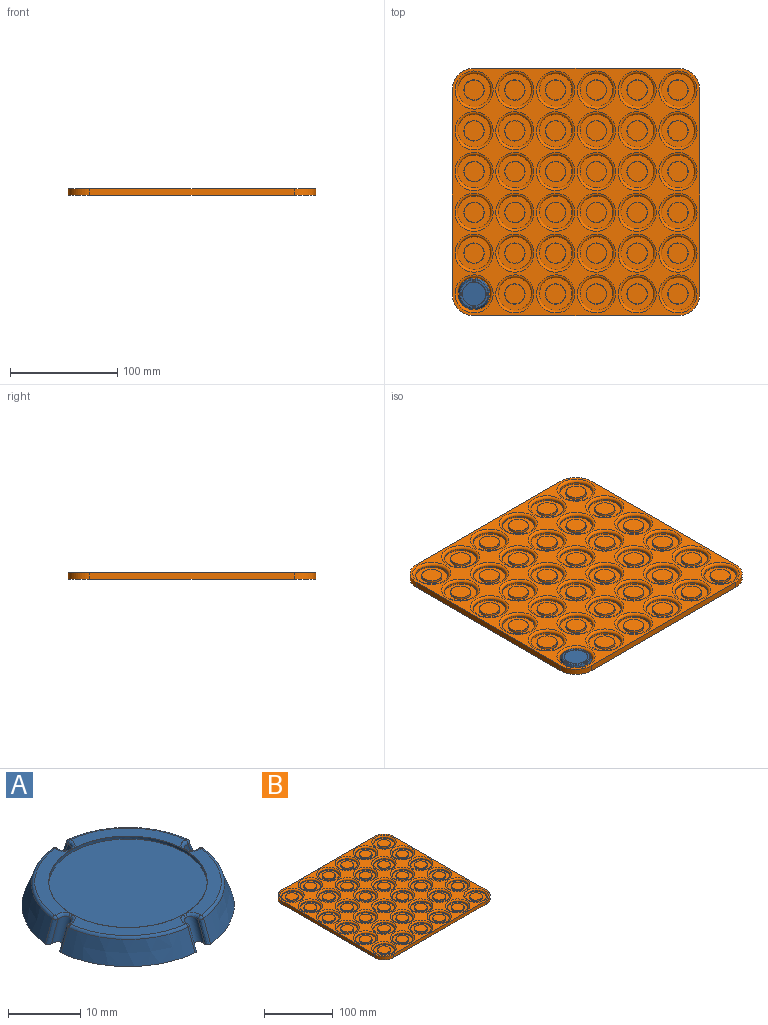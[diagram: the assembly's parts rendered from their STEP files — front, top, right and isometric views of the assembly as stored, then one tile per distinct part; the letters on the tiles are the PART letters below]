
ASSEMBLY  parts=2 mates=1
PART A: 82 faces, bbox 34.2x34.2x13 mm
  f0: cylinder r=3.5mm len=5.05mm, axis (0,-0.34,0.94), area 7.4mm2, adj f1,f32,f33,f34
  f1: bspline ~11.4x4.62mm, area 1.5mm2, adj f0,f2,f31,f34
  f2: sphere r=1mm, area 0.2mm2, adj f1,f3,f32
  f3: torus R=10.66mm, axis (0,0,1), area 13.1mm2, adj f2,f4,f5,f30,f31
  f4: sphere r=1mm, area 0.3mm2, adj f3,f32
  f5: plane 20.32x20.32mm, normal (0,0,-1), area 322.5mm2, adj f3,f6,f24,f25,f27,f28,f29,f32
  f6: torus R=10.66mm, axis (0,0,1), area 13.1mm2, adj f5,f7,f13,f23
  f7: sphere r=1mm, area 0.9mm2, adj f6,f8,f24
  f8: bspline ~11.4x4.62mm, area 1.5mm2, adj f7,f9,f13,f34
  f9: cylinder r=3.5mm len=5.05mm, axis (-0.34,0,0.94), area 7.4mm2, adj f8,f10,f24,f34
  f10: bspline ~11.4x4.62mm, area 1.5mm2, adj f9,f11,f12,f34
  f11: sphere r=1mm, area 0.8mm2, adj f10,f24,f25
  f12: cone r=12.4mm half-angle=20deg, axis (0,0,-1), area 16.4mm2, adj f10,f25,f33,f34
  f13: cone r=12.4mm half-angle=20deg, axis (0,0,-1), area 16.4mm2, adj f6,f8,f14,f34
  f14: bspline ~11.4x4.62mm, area 1.5mm2, adj f13,f15,f23,f34
  f15: cylinder r=3.5mm len=5.05mm, axis (0,0.34,0.94), area 7.4mm2, adj f14,f16,f29,f34
  f16: bspline ~11.4x4.62mm, area 1.5mm2, adj f15,f17,f22,f34
  f17: cone r=12.4mm half-angle=20deg, axis (0,0,-1), area 16.4mm2, adj f16,f18,f28,f34
  f18: bspline ~11.4x4.62mm, area 1.5mm2, adj f17,f19,f21,f34
  f19: cylinder r=3.5mm len=5.05mm, axis (0.34,0,0.94), area 7.4mm2, adj f18,f20,f27,f34
  f20: bspline ~11.4x4.62mm, area 1.5mm2, adj f19,f30,f31,f34
  f21: sphere r=1mm, area 0.4mm2, adj f18,f27,f28
  f22: sphere r=1mm, area 1.2mm2, adj f16,f28,f29
  f23: sphere r=1mm, area 0.4mm2, adj f6,f14,f29
  f24: bspline ~6.46x2.11mm, area 8mm2, adj f5,f7,f9,f11
  f25: torus R=10.66mm, axis (0,0,1), area 13.1mm2, adj f5,f11,f12,f26
  f26: sphere r=1mm, area 0.8mm2, adj f25,f32,f33
  f27: bspline ~6.46x2.11mm, area 8mm2, adj f5,f19,f21,f30
  f28: torus R=10.66mm, axis (0,0,1), area 13.1mm2, adj f5,f17,f21,f22
  f29: bspline ~6.46x2.11mm, area 8mm2, adj f5,f15,f22,f23
  f30: sphere r=1mm, area 1.2mm2, adj f3,f20,f27
  f31: cone r=12.4mm half-angle=20deg, axis (0,0,-1), area 16.4mm2, adj f1,f3,f20,f34
  f32: bspline ~6.46x2.11mm, area 8mm2, adj f0,f2,f4,f5,f26
  f33: bspline ~11.4x4.62mm, area 1.5mm2, adj f0,f12,f26,f34
  f34: plane 30.13x30.13mm, normal (0,0,-1), area 242.1mm2, adj f0,f1,f8,f9,f10,f12,f13,f14
  f35: cylinder r=1mm len=4.47mm, axis (0.34,0,0.94), area 13.2mm2, adj f34,f36,f65,f66,f67,f81
  f36: bspline ~1.87x1.6mm, area 1.4mm2, adj f35,f37,f64,f66
  f37: plane 12.6x12.6mm, normal (0,0,1), area 31.6mm2, adj f36,f38,f60,f63
  f38: bspline ~1.87x1.6mm, area 1.4mm2, adj f37,f39,f40,f78
  f39: sphere r=0.5mm, area 0.5mm2, adj f38,f63,f79
  f40: bspline ~0.76x0.5mm, area 0.2mm2, adj f38,f41,f60,f78
  f41: bspline ~1.87x1.6mm, area 1.4mm2, adj f40,f42,f59,f78
  f42: plane 12.6x12.6mm, normal (0,0,1), area 31.6mm2, adj f41,f43,f45,f60
  f43: torus R=12.94mm, axis (0,0,1), area 10.8mm2, adj f42,f44,f59,f76
  f44: sphere r=0.5mm, area 0.4mm2, adj f43,f45,f75
  f45: bspline ~1.87x1.6mm, area 1.4mm2, adj f42,f44,f46,f74
  f46: bspline ~0.76x0.5mm, area 0.2mm2, adj f45,f47,f60,f74
  f47: bspline ~1.87x1.6mm, area 1.4mm2, adj f46,f48,f58,f74
  f48: plane 12.6x12.6mm, normal (0,0,1), area 31.6mm2, adj f47,f49,f57,f60
  f49: bspline ~1.87x1.6mm, area 1.4mm2, adj f48,f50,f56,f70
  f50: bspline ~0.76x0.5mm, area 0.2mm2, adj f49,f51,f60,f70
  f51: bspline ~1.87x1.6mm, area 1.4mm2, adj f50,f52,f55,f70
  f52: sphere r=0.5mm, area 0.4mm2, adj f51,f53,f69
  f53: torus R=12.94mm, axis (0,0,1), area 10.8mm2, adj f52,f54,f55,f68
  f54: sphere r=0.5mm, area 0.6mm2, adj f53,f65,f67
  f55: plane 12.6x12.6mm, normal (0,0,1), area 31.6mm2, adj f51,f53,f60,f65
  f56: sphere r=0.5mm, area 0.4mm2, adj f49,f57,f71
  f57: torus R=12.94mm, axis (0,0,1), area 10.8mm2, adj f48,f56,f58,f72
  f58: sphere r=0.5mm, area 0.3mm2, adj f47,f57,f73
  f59: sphere r=0.5mm, area 0.5mm2, adj f41,f43,f77
  f60: torus R=0.26mm, axis (0,0,-1), area 1.1mm2, adj f37,f40,f42,f46,f48,f50,f55,f61
  f61: cylinder r=11mm len=22mm, axis (0,0,-1), area 35mm2, adj f60,f62
  f62: plane 22x22mm, normal (0,0,1), area 380.1mm2, adj f61
  f63: torus R=12.94mm, axis (0,0,1), area 10.8mm2, adj f37,f39,f64,f80
  f64: sphere r=0.5mm, area 0.4mm2, adj f36,f63,f81
  f65: bspline ~1.87x1.6mm, area 1.4mm2, adj f35,f54,f55,f66
  f66: bspline ~0.76x0.5mm, area 0.2mm2, adj f35,f36,f60,f65
  f67: bspline ~5.86x2.67mm, area 3.5mm2, adj f34,f35,f54,f68
  f68: cone r=14.75mm half-angle=20deg, axis (0,0,-1), area 74.4mm2, adj f34,f53,f67,f69
  f69: bspline ~10.56x4.38mm, area 3.5mm2, adj f34,f52,f68,f70
  f70: cylinder r=1mm len=4.47mm, axis (0,0.34,0.94), area 13.2mm2, adj f34,f49,f50,f51,f69,f71
  f71: bspline ~5.86x2.67mm, area 3.5mm2, adj f34,f56,f70,f72
  f72: cone r=14.75mm half-angle=20deg, axis (0,0,-1), area 74.4mm2, adj f34,f57,f71,f73
  f73: bspline ~10.56x4.38mm, area 3.5mm2, adj f34,f58,f72,f74
  f74: cylinder r=1mm len=4.47mm, axis (-0.34,0,0.94), area 13.2mm2, adj f34,f45,f46,f47,f73,f75
  f75: bspline ~5.86x2.67mm, area 3.5mm2, adj f34,f44,f74,f76
  f76: cone r=14.75mm half-angle=20deg, axis (0,0,-1), area 74.4mm2, adj f34,f43,f75,f77
  f77: bspline ~10.56x4.38mm, area 3.5mm2, adj f34,f59,f76,f78
  f78: cylinder r=1mm len=4.47mm, axis (0,-0.34,0.94), area 13.2mm2, adj f34,f38,f40,f41,f77,f79
  f79: bspline ~5.86x2.67mm, area 3.5mm2, adj f34,f39,f78,f80
  f80: cone r=14.75mm half-angle=20deg, axis (0,0,-1), area 74.4mm2, adj f34,f63,f79,f81
  f81: bspline ~10.56x4.38mm, area 3.5mm2, adj f34,f35,f64,f80
PART B: 190 faces, bbox 230.5x232.3x6 mm
  f0: plane 190.5x6mm, normal (-1,0,0), area 1143mm2, adj f40,f41,f186,f189
  f1: plane 190.5x6mm, normal (0,-1,0), area 1143mm2, adj f40,f41,f186,f187
  f2: plane 190.5x6mm, normal (1,0,0), area 1143mm2, adj f40,f41,f187,f188
  f3: cylinder r=15.25mm len=30.5mm, axis (0,0,-1), area 143.7mm2, adj f76,f150
  f4: cylinder r=15.25mm len=30.5mm, axis (0,0,-1), area 143.7mm2, adj f75,f151
  f5: cylinder r=15.25mm len=30.5mm, axis (0,0,-1), area 143.7mm2, adj f74,f152
  f6: cylinder r=15.25mm len=30.5mm, axis (0,0,-1), area 143.7mm2, adj f73,f153
  f7: cylinder r=15.25mm len=30.5mm, axis (0,0,-1), area 143.7mm2, adj f72,f154
  f8: cylinder r=15.25mm len=30.5mm, axis (0,0,-1), area 143.7mm2, adj f71,f155
  f9: cylinder r=15.25mm len=30.5mm, axis (0,0,-1), area 143.7mm2, adj f70,f156
  f10: cylinder r=15.25mm len=30.5mm, axis (0,0,-1), area 143.7mm2, adj f69,f157
  f11: cylinder r=15.25mm len=30.5mm, axis (0,0,-1), area 143.7mm2, adj f68,f158
  f12: cylinder r=15.25mm len=30.5mm, axis (0,0,-1), area 143.7mm2, adj f67,f159
  f13: cylinder r=15.25mm len=30.5mm, axis (0,0,-1), area 143.7mm2, adj f66,f160
  f14: cylinder r=15.25mm len=30.5mm, axis (0,0,-1), area 143.7mm2, adj f65,f161
  f15: cylinder r=15.25mm len=30.5mm, axis (0,0,-1), area 143.7mm2, adj f64,f162
  f16: cylinder r=15.25mm len=30.5mm, axis (0,0,-1), area 143.7mm2, adj f63,f163
  f17: cylinder r=15.25mm len=30.5mm, axis (0,0,-1), area 143.7mm2, adj f62,f164
  f18: cylinder r=15.25mm len=30.5mm, axis (0,0,-1), area 143.7mm2, adj f61,f165
  f19: cylinder r=15.25mm len=30.5mm, axis (0,0,-1), area 143.7mm2, adj f60,f166
  f20: cylinder r=15.25mm len=30.5mm, axis (0,0,-1), area 143.7mm2, adj f59,f167
  f21: cylinder r=15.25mm len=30.5mm, axis (0,0,-1), area 143.7mm2, adj f58,f168
  f22: cylinder r=15.25mm len=30.5mm, axis (0,0,-1), area 143.7mm2, adj f57,f169
  f23: cylinder r=15.25mm len=30.5mm, axis (0,0,-1), area 143.7mm2, adj f56,f170
  f24: cylinder r=15.25mm len=30.5mm, axis (0,0,-1), area 143.7mm2, adj f55,f171
  f25: cylinder r=15.25mm len=30.5mm, axis (0,0,-1), area 143.7mm2, adj f54,f172
  f26: cylinder r=15.25mm len=30.5mm, axis (0,0,-1), area 143.7mm2, adj f53,f173
  f27: cylinder r=15.25mm len=30.5mm, axis (0,0,-1), area 143.7mm2, adj f52,f174
  f28: cylinder r=15.25mm len=30.5mm, axis (0,0,-1), area 143.7mm2, adj f51,f175
  f29: cylinder r=15.25mm len=30.5mm, axis (0,0,-1), area 143.7mm2, adj f50,f176
  f30: cylinder r=15.25mm len=30.5mm, axis (0,0,-1), area 143.7mm2, adj f49,f177
  f31: cylinder r=15.25mm len=30.5mm, axis (0,0,-1), area 143.7mm2, adj f48,f178
  f32: cylinder r=15.25mm len=30.5mm, axis (0,0,-1), area 143.7mm2, adj f47,f179
  f33: cylinder r=15.25mm len=30.5mm, axis (0,0,-1), area 143.7mm2, adj f46,f180
  f34: cylinder r=15.25mm len=30.5mm, axis (0,0,-1), area 143.7mm2, adj f45,f181
  f35: cylinder r=15.25mm len=30.5mm, axis (0,0,-1), area 143.7mm2, adj f44,f182
  f36: cylinder r=15.25mm len=30.5mm, axis (0,0,-1), area 143.7mm2, adj f43,f183
  f37: cylinder r=15.25mm len=30.5mm, axis (0,0,-1), area 143.7mm2, adj f42,f184
  f38: plane 190.5x6mm, normal (0,1,0), area 1143mm2, adj f40,f41,f188,f189
  f39: cylinder r=15.25mm len=30.5mm, axis (0,0,-1), area 143.7mm2, adj f77,f185
  f40: plane 230.5x230.5mm, normal (0,0,1), area 17154.2mm2, adj f0,f1,f2,f38,f150,f151,f152,f153
  f41: plane 230.5x230.5mm, normal (0,0,-1), area 52786.9mm2, adj f0,f1,f2,f38,f186,f187,f188,f189
  f42: plane 30.5x30.5mm, normal (0,0,1), area 447.1mm2, adj f37,f79
  f43: plane 30.5x30.5mm, normal (0,0,1), area 447.1mm2, adj f36,f81
  f44: plane 30.5x30.5mm, normal (0,0,1), area 447.1mm2, adj f35,f83
  f45: plane 30.5x30.5mm, normal (0,0,1), area 447.1mm2, adj f34,f85
  f46: plane 30.5x30.5mm, normal (0,0,1), area 447.1mm2, adj f33,f87
  f47: plane 30.5x30.5mm, normal (0,0,1), area 447.1mm2, adj f32,f89
  f48: plane 30.5x30.5mm, normal (0,0,1), area 447.1mm2, adj f31,f91
  f49: plane 30.5x30.5mm, normal (0,0,1), area 447.1mm2, adj f30,f93
  f50: plane 30.5x30.5mm, normal (0,0,1), area 447.1mm2, adj f29,f95
  f51: plane 30.5x30.5mm, normal (0,0,1), area 447.1mm2, adj f28,f97
  f52: plane 30.5x30.5mm, normal (0,0,1), area 447.1mm2, adj f27,f99
  f53: plane 30.5x30.5mm, normal (0,0,1), area 447.1mm2, adj f26,f101
  f54: plane 30.5x30.5mm, normal (0,0,1), area 447.1mm2, adj f25,f103
  f55: plane 30.5x30.5mm, normal (0,0,1), area 447.1mm2, adj f24,f105
  f56: plane 30.5x30.5mm, normal (0,0,1), area 447.1mm2, adj f23,f107
  f57: plane 30.5x30.5mm, normal (0,0,1), area 447.1mm2, adj f22,f109
  f58: plane 30.5x30.5mm, normal (0,0,1), area 447.1mm2, adj f21,f111
  f59: plane 30.5x30.5mm, normal (0,0,1), area 447.1mm2, adj f20,f113
  f60: plane 30.5x30.5mm, normal (0,0,1), area 447.1mm2, adj f19,f115
  f61: plane 30.5x30.5mm, normal (0,0,1), area 447.1mm2, adj f18,f117
  f62: plane 30.5x30.5mm, normal (0,0,1), area 447.1mm2, adj f17,f119
  f63: plane 30.5x30.5mm, normal (0,0,1), area 447.1mm2, adj f16,f121
  f64: plane 30.5x30.5mm, normal (0,0,1), area 447.1mm2, adj f15,f123
  f65: plane 30.5x30.5mm, normal (0,0,1), area 447.1mm2, adj f14,f125
  f66: plane 30.5x30.5mm, normal (0,0,1), area 447.1mm2, adj f13,f127
  f67: plane 30.5x30.5mm, normal (0,0,1), area 447.1mm2, adj f12,f129
  f68: plane 30.5x30.5mm, normal (0,0,1), area 447.1mm2, adj f11,f131
  f69: plane 30.5x30.5mm, normal (0,0,1), area 447.1mm2, adj f10,f133
  f70: plane 30.5x30.5mm, normal (0,0,1), area 447.1mm2, adj f9,f135
  f71: plane 30.5x30.5mm, normal (0,0,1), area 447.1mm2, adj f8,f137
  f72: plane 30.5x30.5mm, normal (0,0,1), area 447.1mm2, adj f7,f139
  f73: plane 30.5x30.5mm, normal (0,0,1), area 447.1mm2, adj f6,f141
  f74: plane 30.5x30.5mm, normal (0,0,1), area 447.1mm2, adj f5,f143
  f75: plane 30.5x30.5mm, normal (0,0,1), area 447.1mm2, adj f4,f145
  f76: plane 30.5x30.5mm, normal (0,0,1), area 447.1mm2, adj f3,f147
  f77: plane 30.5x30.5mm, normal (0,0,1), area 447.1mm2, adj f39,f149
  f78: plane 18.58x18.58mm, normal (0,0,1), area 271.1mm2, adj f79
  f79: cone r=9.5mm half-angle=6deg, axis (0,0,-1), area 118.7mm2, adj f42,f78
  f80: plane 18.58x18.58mm, normal (0,0,1), area 271.1mm2, adj f81
  f81: cone r=9.5mm half-angle=6deg, axis (0,0,-1), area 118.7mm2, adj f43,f80
  f82: plane 18.58x18.58mm, normal (0,0,1), area 271.1mm2, adj f83
  f83: cone r=9.5mm half-angle=6deg, axis (0,0,-1), area 118.7mm2, adj f44,f82
  f84: plane 18.58x18.58mm, normal (0,0,1), area 271.1mm2, adj f85
  f85: cone r=9.5mm half-angle=6deg, axis (0,0,-1), area 118.7mm2, adj f45,f84
  f86: plane 18.58x18.58mm, normal (0,0,1), area 271.1mm2, adj f87
  f87: cone r=9.5mm half-angle=6deg, axis (0,0,-1), area 118.7mm2, adj f46,f86
  f88: plane 18.58x18.58mm, normal (0,0,1), area 271.1mm2, adj f89
  f89: cone r=9.5mm half-angle=6deg, axis (0,0,-1), area 118.7mm2, adj f47,f88
  f90: plane 18.58x18.58mm, normal (0,0,1), area 271.1mm2, adj f91
  f91: cone r=9.5mm half-angle=6deg, axis (0,0,-1), area 118.7mm2, adj f48,f90
  f92: plane 18.58x18.58mm, normal (0,0,1), area 271.1mm2, adj f93
  f93: cone r=9.5mm half-angle=6deg, axis (0,0,-1), area 118.7mm2, adj f49,f92
  f94: plane 18.58x18.58mm, normal (0,0,1), area 271.1mm2, adj f95
  f95: cone r=9.5mm half-angle=6deg, axis (0,0,-1), area 118.7mm2, adj f50,f94
  f96: plane 18.58x18.58mm, normal (0,0,1), area 271.1mm2, adj f97
  f97: cone r=9.5mm half-angle=6deg, axis (0,0,-1), area 118.7mm2, adj f51,f96
  f98: plane 18.58x18.58mm, normal (0,0,1), area 271.1mm2, adj f99
  f99: cone r=9.5mm half-angle=6deg, axis (0,0,-1), area 118.7mm2, adj f52,f98
  f100: plane 18.58x18.58mm, normal (0,0,1), area 271.1mm2, adj f101
  f101: cone r=9.5mm half-angle=6deg, axis (0,0,-1), area 118.7mm2, adj f53,f100
  f102: plane 18.58x18.58mm, normal (0,0,1), area 271.1mm2, adj f103
  f103: cone r=9.5mm half-angle=6deg, axis (0,0,-1), area 118.7mm2, adj f54,f102
  f104: plane 18.58x18.58mm, normal (0,0,1), area 271.1mm2, adj f105
  f105: cone r=9.5mm half-angle=6deg, axis (0,0,-1), area 118.7mm2, adj f55,f104
  f106: plane 18.58x18.58mm, normal (0,0,1), area 271.1mm2, adj f107
  f107: cone r=9.5mm half-angle=6deg, axis (0,0,-1), area 118.7mm2, adj f56,f106
  f108: plane 18.58x18.58mm, normal (0,0,1), area 271.1mm2, adj f109
  f109: cone r=9.5mm half-angle=6deg, axis (0,0,-1), area 118.7mm2, adj f57,f108
  f110: plane 18.58x18.58mm, normal (0,0,1), area 271.1mm2, adj f111
  f111: cone r=9.5mm half-angle=6deg, axis (0,0,-1), area 118.7mm2, adj f58,f110
  f112: plane 18.58x18.58mm, normal (0,0,1), area 271.1mm2, adj f113
  f113: cone r=9.5mm half-angle=6deg, axis (0,0,-1), area 118.7mm2, adj f59,f112
  f114: plane 18.58x18.58mm, normal (0,0,1), area 271.1mm2, adj f115
  f115: cone r=9.5mm half-angle=6deg, axis (0,0,-1), area 118.7mm2, adj f60,f114
  f116: plane 18.58x18.58mm, normal (0,0,1), area 271.1mm2, adj f117
  f117: cone r=9.5mm half-angle=6deg, axis (0,0,-1), area 118.7mm2, adj f61,f116
  f118: plane 18.58x18.58mm, normal (0,0,1), area 271.1mm2, adj f119
  f119: cone r=9.5mm half-angle=6deg, axis (0,0,-1), area 118.7mm2, adj f62,f118
  f120: plane 18.58x18.58mm, normal (0,0,1), area 271.1mm2, adj f121
  f121: cone r=9.5mm half-angle=6deg, axis (0,0,-1), area 118.7mm2, adj f63,f120
  f122: plane 18.58x18.58mm, normal (0,0,1), area 271.1mm2, adj f123
  f123: cone r=9.5mm half-angle=6deg, axis (0,0,-1), area 118.7mm2, adj f64,f122
  f124: plane 18.58x18.58mm, normal (0,0,1), area 271.1mm2, adj f125
  f125: cone r=9.5mm half-angle=6deg, axis (0,0,-1), area 118.7mm2, adj f65,f124
  f126: plane 18.58x18.58mm, normal (0,0,1), area 271.1mm2, adj f127
  f127: cone r=9.5mm half-angle=6deg, axis (0,0,-1), area 118.7mm2, adj f66,f126
  f128: plane 18.58x18.58mm, normal (0,0,1), area 271.1mm2, adj f129
  f129: cone r=9.5mm half-angle=6deg, axis (0,0,-1), area 118.7mm2, adj f67,f128
  f130: plane 18.58x18.58mm, normal (0,0,1), area 271.1mm2, adj f131
  f131: cone r=9.5mm half-angle=6deg, axis (0,0,-1), area 118.7mm2, adj f68,f130
  f132: plane 18.58x18.58mm, normal (0,0,1), area 271.1mm2, adj f133
  f133: cone r=9.5mm half-angle=6deg, axis (0,0,-1), area 118.7mm2, adj f69,f132
  f134: plane 18.58x18.58mm, normal (0,0,1), area 271.1mm2, adj f135
  f135: cone r=9.5mm half-angle=6deg, axis (0,0,-1), area 118.7mm2, adj f70,f134
  f136: plane 18.58x18.58mm, normal (0,0,1), area 271.1mm2, adj f137
  f137: cone r=9.5mm half-angle=6deg, axis (0,0,-1), area 118.7mm2, adj f71,f136
  f138: plane 18.58x18.58mm, normal (0,0,1), area 271.1mm2, adj f139
  f139: cone r=9.5mm half-angle=6deg, axis (0,0,-1), area 118.7mm2, adj f72,f138
  f140: plane 18.58x18.58mm, normal (0,0,1), area 271.1mm2, adj f141
  f141: cone r=9.5mm half-angle=6deg, axis (0,0,-1), area 118.7mm2, adj f73,f140
  f142: plane 18.58x18.58mm, normal (0,0,1), area 271.1mm2, adj f143
  f143: cone r=9.5mm half-angle=6deg, axis (0,0,-1), area 118.7mm2, adj f74,f142
  f144: plane 18.58x18.58mm, normal (0,0,1), area 271.1mm2, adj f145
  f145: cone r=9.5mm half-angle=6deg, axis (0,0,-1), area 118.7mm2, adj f75,f144
  f146: plane 18.58x18.58mm, normal (0,0,1), area 271.1mm2, adj f147
  f147: cone r=9.5mm half-angle=6deg, axis (0,0,-1), area 118.7mm2, adj f76,f146
  f148: plane 18.58x18.58mm, normal (0,0,1), area 271.1mm2, adj f149
  f149: cone r=9.5mm half-angle=6deg, axis (0,0,-1), area 118.7mm2, adj f77,f148
  f150: torus R=17.75mm, axis (0,0,1), area 398.7mm2, adj f3,f40
  f151: torus R=17.75mm, axis (0,0,1), area 398.7mm2, adj f4,f40
  f152: torus R=17.75mm, axis (0,0,1), area 398.7mm2, adj f5,f40
  f153: torus R=17.75mm, axis (0,0,1), area 398.7mm2, adj f6,f40
  f154: torus R=17.75mm, axis (0,0,1), area 398.7mm2, adj f7,f40
  f155: torus R=17.75mm, axis (0,0,1), area 398.7mm2, adj f8,f40
  f156: torus R=17.75mm, axis (0,0,1), area 398.7mm2, adj f9,f40
  f157: torus R=17.75mm, axis (0,0,1), area 398.7mm2, adj f10,f40
  f158: torus R=17.75mm, axis (0,0,1), area 398.7mm2, adj f11,f40
  f159: torus R=17.75mm, axis (0,0,1), area 398.7mm2, adj f12,f40
  f160: torus R=17.75mm, axis (0,0,1), area 398.7mm2, adj f13,f40
  f161: torus R=17.75mm, axis (0,0,1), area 398.7mm2, adj f14,f40
  f162: torus R=17.75mm, axis (0,0,1), area 398.7mm2, adj f15,f40
  f163: torus R=17.75mm, axis (0,0,1), area 398.7mm2, adj f16,f40
  f164: torus R=17.75mm, axis (0,0,1), area 398.7mm2, adj f17,f40
  f165: torus R=17.75mm, axis (0,0,1), area 398.7mm2, adj f18,f40
  f166: torus R=17.75mm, axis (0,0,1), area 398.7mm2, adj f19,f40
  f167: torus R=17.75mm, axis (0,0,1), area 398.7mm2, adj f20,f40
  f168: torus R=17.75mm, axis (0,0,1), area 398.7mm2, adj f21,f40
  f169: torus R=17.75mm, axis (0,0,1), area 398.7mm2, adj f22,f40
  f170: torus R=17.75mm, axis (0,0,1), area 398.7mm2, adj f23,f40
  f171: torus R=17.75mm, axis (0,0,1), area 398.7mm2, adj f24,f40
  f172: torus R=17.75mm, axis (0,0,1), area 398.7mm2, adj f25,f40
  f173: torus R=17.75mm, axis (0,0,1), area 398.7mm2, adj f26,f40
  f174: torus R=17.75mm, axis (0,0,1), area 398.7mm2, adj f27,f40
  f175: torus R=17.75mm, axis (0,0,1), area 398.7mm2, adj f28,f40
  f176: torus R=17.75mm, axis (0,0,1), area 398.7mm2, adj f29,f40
  f177: torus R=17.75mm, axis (0,0,1), area 398.7mm2, adj f30,f40
  f178: torus R=17.75mm, axis (0,0,1), area 398.7mm2, adj f31,f40
  f179: torus R=17.75mm, axis (0,0,1), area 398.7mm2, adj f32,f40
  f180: torus R=17.75mm, axis (0,0,1), area 398.7mm2, adj f33,f40
  f181: torus R=17.75mm, axis (0,0,1), area 398.7mm2, adj f34,f40
  f182: torus R=17.75mm, axis (0,0,1), area 398.7mm2, adj f35,f40
  f183: torus R=17.75mm, axis (0,0,1), area 398.7mm2, adj f36,f40
  f184: torus R=17.75mm, axis (0,0,1), area 398.7mm2, adj f37,f40
  f185: torus R=17.75mm, axis (0,0,1), area 398.7mm2, adj f39,f40
  f186: cylinder r=20mm len=20mm, axis (0,0,1), area 188.5mm2, adj f0,f1,f40,f41
  f187: cylinder r=20mm len=20mm, axis (0,0,-1), area 188.5mm2, adj f1,f2,f40,f41
  f188: cylinder r=20mm len=20mm, axis (0,0,1), area 188.5mm2, adj f2,f38,f40,f41
  f189: cylinder r=20mm len=20mm, axis (0,0,-1), area 188.5mm2, adj f0,f38,f40,f41
PLACE A t=(0,0,26.2)mm
PLACE B t=(0,0,24.2)mm
MATE planar B.f37 <-> A.f3  axis (0,0,1) through (0,0,26.2)mm
